FCSTD DOCUMENT  (FreeCAD 0.20R29603 (Git))
Label: outline
License: All rights reserved
LicenseURL: http://en.wikipedia.org/wiki/All_rights_reserved
objects: Sketcher::SketchObject×1
note: 1 computed .brp shape members not serialized (recipe doc carries the construction recipe); baked Part::Feature solids carry a one-line shape summary decoded from their .brp

FEATURE [Sketcher::SketchObject] Sketch
  FullyConstrained = true
  sketch-geometry (14):
    g0: ArcOfCircle CenterX=-29 CenterY=29 CenterZ=0 NormalX=0 NormalY=0 NormalZ=1 AngleXU=0 Radius=6 StartAngle=1.5708 EndAngle=3.14159
    g1: LineSegment StartX=-29 StartY=35 StartZ=0 EndX=29 EndY=35 EndZ=0
    g2: ArcOfCircle CenterX=29 CenterY=29 CenterZ=0 NormalX=0 NormalY=0 NormalZ=1 AngleXU=0 Radius=6 StartAngle=5.36e-14 EndAngle=1.5708
    g3: LineSegment StartX=35 StartY=29 StartZ=0 EndX=35 EndY=-29 EndZ=0
    g4: ArcOfCircle CenterX=29 CenterY=-29 CenterZ=0 NormalX=0 NormalY=0 NormalZ=1 AngleXU=0 Radius=6 StartAngle=4.71239 EndAngle=6.28319
    g5: LineSegment StartX=29 StartY=-35 StartZ=0 EndX=-29 EndY=-35 EndZ=0
    g6: ArcOfCircle CenterX=-29 CenterY=-29 CenterZ=0 NormalX=0 NormalY=0 NormalZ=1 AngleXU=0 Radius=6 StartAngle=3.14159 EndAngle=4.71239
    g7: LineSegment StartX=-35 StartY=-29 StartZ=0 EndX=-35 EndY=29 EndZ=0
    g8: GeomPoint X=-35 Y=35 Z=0
    g9: GeomPoint X=35 Y=-35 Z=0
    g10: Circle CenterX=-29 CenterY=-29 CenterZ=0 NormalX=0 NormalY=0 NormalZ=1 AngleXU=0 Radius=3
    g11: Circle CenterX=29 CenterY=-29 CenterZ=0 NormalX=0 NormalY=0 NormalZ=1 AngleXU=0 Radius=3
    g12: Circle CenterX=29 CenterY=29 CenterZ=0 NormalX=0 NormalY=0 NormalZ=1 AngleXU=0 Radius=3
    g13: Circle CenterX=-29 CenterY=29 CenterZ=0 NormalX=0 NormalY=0 NormalZ=1 AngleXU=0 Radius=3
  constraints (32):
    c: Tangent(g0,g1) = 1.5708
    c: Tangent(g1,g2) = 1.5708
    c: Tangent(g2,g3) = 1.5708
    c: Tangent(g3,g4) = 1.5708
    c: Tangent(g4,g5) = 1.5708
    c: Tangent(g5,g6) = 1.5708
    c: Tangent(g6,g7) = 1.5708
    c: Tangent(g7,g0) = 1.5708
    c: Horizontal(g1)
    c: Horizontal(g5)
    c: Vertical(g3)
    c: Vertical(g7)
    c: Equal(g0,g2)
    c: Equal(g2,g4)
    c: Equal(g4,g6)
    c: PointOnObject(g8,g1)
    c: PointOnObject(g8,g7)
    c: PointOnObject(g9,g3)
    c: PointOnObject(g9,g5)
    c: DistanceX(g1,g1) = 58
    c: DistanceY(g7,g7) = 58
    c: Radius(g0) = 6
    c: Coincident(g10,g6)
    c: Coincident(g11,g4)
    c: Coincident(g12,g2)
    c: Coincident(g13,g0)
    c: Diameter(g13) = 6
    c: Diameter(g12) = 6
    c: Diameter(g11) = 6
    c: Diameter(g10) = 6
    c: DistanceY(g-1,g0) = 35
    c: DistanceX(g-1,g2) = 35
